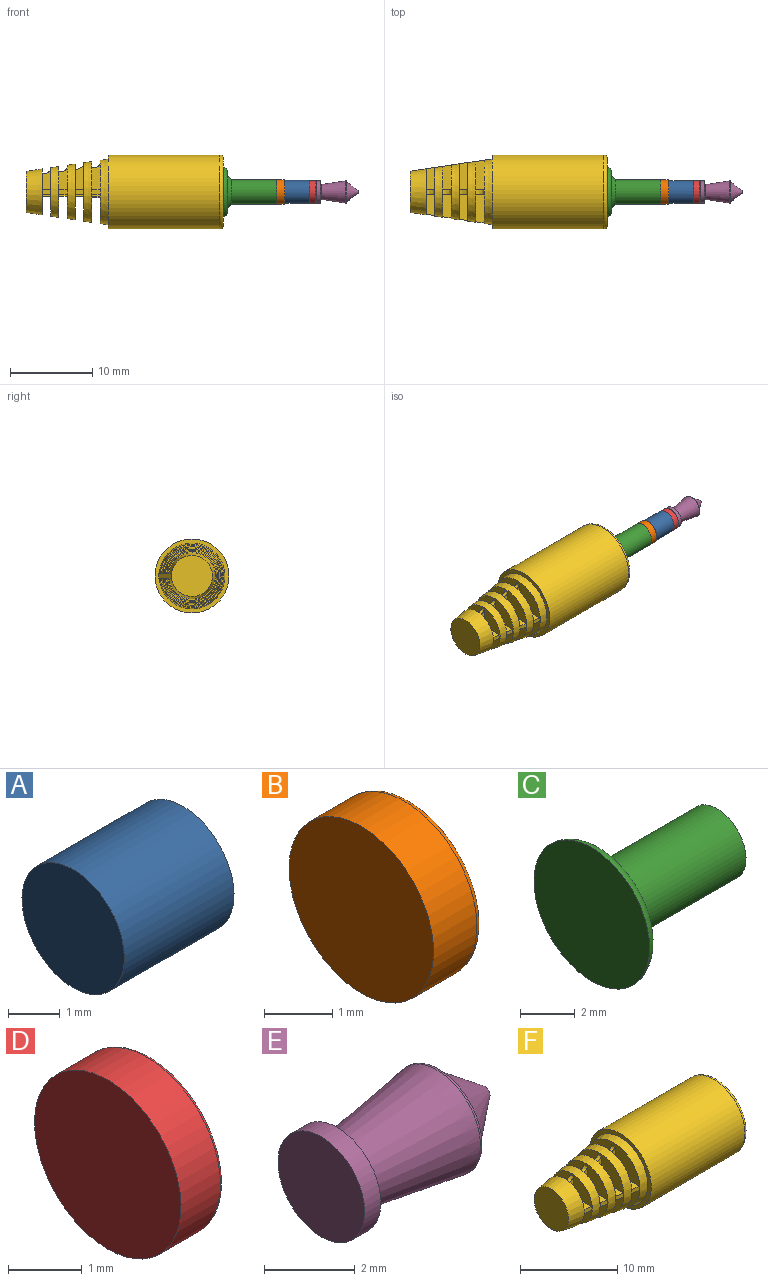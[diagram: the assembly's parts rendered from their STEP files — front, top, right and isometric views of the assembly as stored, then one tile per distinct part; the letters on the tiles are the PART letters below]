
ASSEMBLY  parts=6 mates=5
PART A: 3 faces, bbox 3x2.8x2.8 mm
  f0: cylinder r=1.4mm len=3mm, axis (-1,0,0), area 26.4mm2, adj f1,f2
  f1: plane 2.8x2.8mm, normal (1,0,0), area 6.2mm2, adj f0
  f2: plane 2.8x2.8mm, normal (-1,0,0), area 6.2mm2, adj f0
PART B: 4 faces, bbox 1x3.2x3.2 mm
  f0: cylinder r=1.5mm len=3mm, axis (-1,0,0), area 8.5mm2, adj f2,f3
  f1: plane 2.8x2.8mm, normal (1,0,0), area 6.2mm2, adj f3
  f2: plane 3x3mm, normal (-1,0,0), area 7.1mm2, adj f0
  f3: torus R=1.4mm, axis (1,0,0), area 1.4mm2, adj f0,f1
PART C: 6 faces, bbox 6.6x6.5x6.5 mm
  f0: plane 4.9x4.9mm, normal (1,0,0), area 6.3mm2, adj f4,f5
  f1: plane 6x6mm, normal (-1,0,0), area 28.3mm2, adj f4
  f2: cylinder r=1.5mm len=5.5mm, axis (-1,0,0), area 51.8mm2, adj f3,f5
  f3: plane 3x3mm, normal (1,0,0), area 7.1mm2, adj f2
  f4: torus R=2.45mm, axis (-1,0,0), area 14.3mm2, adj f0,f1
  f5: cone r=1.5mm half-angle=45deg, axis (-1,0,0), area 7.8mm2, adj f0,f2
PART D: 4 faces, bbox 0.8x3x3 mm
  f0: cylinder r=1.4mm len=2.8mm, axis (-1,0,0), area 6.6mm2, adj f2,f3
  f1: plane 2.7x2.7mm, normal (1,0,0), area 5.7mm2, adj f3
  f2: plane 2.8x2.8mm, normal (-1,0,0), area 6.2mm2, adj f0
  f3: torus R=1.35mm, axis (1,0,0), area 0.7mm2, adj f0,f1
PART E: 8 faces, bbox 5.1x2.7x2.7 mm
  f0: plane 2.7x2.7mm, normal (-1,0,0), area 5.7mm2, adj f7
  f1: plane 0.3x0.3mm, normal (1,0,0), area 0.1mm2, adj f2
  f2: cone r=1.28mm half-angle=37.9deg, axis (-1,0,0), area 8.3mm2, adj f1,f3
  f3: plane 2.7x2.7mm, normal (1,0,0), area 0.6mm2, adj f2,f4
  f4: cylinder r=1.35mm len=2.7mm, axis (-1,0,0), area 0.4mm2, adj f3,f5
  f5: cone r=1.35mm half-angle=8.5deg, axis (1,0,0), area 21.4mm2, adj f4,f6
  f6: cone r=1.35mm half-angle=77.5deg, axis (-1,0,0), area 3.3mm2, adj f5,f7
  f7: cylinder r=1.35mm len=2.7mm, axis (-1,0,0), area 4.2mm2, adj f0,f6
PART F: 63 faces, bbox 24x9.7x9.7 mm
  f0: plane 1.01x0.5mm, normal (-0.15,-0.99,0), area 0.5mm2, adj f1,f2,f50,f59
  f1: plane 9.86x6.9mm, normal (0,0,1), area 15.3mm2, adj f0,f28,f32,f33,f35,f38,f39,f42
  f2: plane 9.86x6.9mm, normal (0,0,-1), area 15.3mm2, adj f0,f23,f24,f25,f26,f27,f28,f32
  f3: plane 1x0.14mm, normal (0,-1,0), area 0.1mm2, adj f5,f15,f35,f39
  f4: plane 1x0.14mm, normal (0,1,0), area 0.1mm2, adj f5,f16,f35,f39
  f5: plane 1x0.23mm, normal (0,0,-1), area 0.2mm2, adj f3,f4,f35,f39
  f6: plane 1x0.5mm, normal (-0.15,-0.99,0), area 0.5mm2, adj f11,f12,f35,f39
  f7: plane 1x0.5mm, normal (-0.15,-0.99,0), area 0.5mm2, adj f9,f13,f47,f51
  f8: plane 1.02x0.5mm, normal (-0.15,-0.99,0), area 0.5mm2, adj f10,f14,f48,f52
  f9: plane 2.92x1mm, normal (0,0,1), area 2.8mm2, adj f7,f44,f47,f51
  f10: plane 3.22x1.02mm, normal (0,0,1), area 3.2mm2, adj f8,f41,f48,f52
  f11: plane 3.52x1mm, normal (0,0,1), area 3.4mm2, adj f6,f35,f37,f39
  f12: plane 3.52x1mm, normal (0,0,-1), area 3.4mm2, adj f6,f20,f35,f39
  f13: plane 2.92x1mm, normal (0,0,-1), area 2.8mm2, adj f7,f21,f47,f51
  f14: plane 3.22x1.02mm, normal (0,0,-1), area 3.2mm2, adj f8,f22,f48,f52
  f15: plane 1x0.25mm, normal (0,0,-1), area 0.3mm2, adj f3,f20,f35,f39
  f16: plane 1x0.02mm, normal (0,0,-1), area 0mm2, adj f4,f24,f35,f39
  f17: plane 1x0.5mm, normal (0,0,-1), area 0.5mm2, adj f21,f25,f47,f51
  f18: plane 1.02x0.5mm, normal (0,0,-1), area 0.5mm2, adj f22,f26,f48,f52
  f19: plane 0.99x0.5mm, normal (0,0,-1), area 0.5mm2, adj f23,f27,f34,f50
  f20: plane 1x0.3mm, normal (0,-1,0), area 0.3mm2, adj f12,f15,f35,f39
  f21: plane 1x0.3mm, normal (0,-1,0), area 0.3mm2, adj f13,f17,f47,f51
  f22: plane 1.02x0.3mm, normal (0,-1,0), area 0.3mm2, adj f14,f18,f48,f52
  f23: plane 0.99x0.3mm, normal (0,-1,0), area 0.3mm2, adj f2,f19,f34,f50
  f24: plane 1x0.3mm, normal (0,1,0), area 0.3mm2, adj f2,f16,f35,f39
  f25: plane 1x0.3mm, normal (0,1,0), area 0.3mm2, adj f2,f17,f47,f51
  f26: plane 1.02x0.3mm, normal (0,1,0), area 0.3mm2, adj f2,f18,f48,f52
  f27: plane 0.99x0.3mm, normal (0,1,0), area 0.3mm2, adj f2,f19,f34,f50
  f28: plane 9x9mm, normal (-1,0,0), area 13.3mm2, adj f1,f2,f29,f32,f54
  f29: cylinder r=4.5mm len=13.6mm, axis (1,0,0), area 384.5mm2, adj f28,f31
  f30: plane 8.2x8.2mm, normal (1,0,0), area 52.8mm2, adj f31
  f31: torus R=4.1mm, axis (1,0,0), area 17.2mm2, adj f29,f30
  f32: plane 9.85x1.48mm, normal (-0.15,0.99,0), area 5mm2, adj f1,f2,f28,f33
  f33: plane 0.5x0.04mm, normal (-1,0,0), area 0mm2, adj f1,f2,f32,f61
  f34: plane 0.5x0.3mm, normal (-1,0,0), area 0.2mm2, adj f2,f19,f23,f27
  f35: plane 7.7x7.69mm, normal (-1,0,0), area 40.9mm2, adj f1,f2,f3,f4,f5,f6,f11,f12
  f36: extruded ~1x0.52mm, area 0.6mm2, adj f35,f37,f38,f39
  f37: plane 3.25x1mm, normal (0,-1,0), area 2.8mm2, adj f11,f35,f36,f39
  f38: plane 3.25x1mm, normal (0,1,0), area 2.8mm2, adj f1,f35,f36,f39
  f39: plane 7.4x7.39mm, normal (1,0,0), area 37.8mm2, adj f1,f2,f3,f4,f5,f6,f11,f12
  f40: extruded ~1.02x0.51mm, area 0.6mm2, adj f41,f42,f48,f52
  f41: plane 3x1.02mm, normal (0,-1,0), area 2.7mm2, adj f10,f40,f48,f52
  f42: plane 3x1.02mm, normal (0,1,0), area 2.7mm2, adj f1,f40,f48,f52
  f43: extruded ~1x0.51mm, area 0.6mm2, adj f44,f45,f47,f51
  f44: plane 2.75x1mm, normal (0,-1,0), area 2.3mm2, adj f9,f43,f47,f51
  f45: plane 2.75x1mm, normal (0,1,0), area 2.3mm2, adj f1,f43,f47,f51
  f46: cone r=3.4mm half-angle=8.5deg, axis (1,0,0), area 20.6mm2, adj f1,f2,f47,f48
  f47: plane 6.5x6.49mm, normal (-1,0,0), area 28.4mm2, adj f1,f2,f7,f9,f13,f17,f21,f25
  f48: plane 6.8x6.79mm, normal (1,0,0), area 31.6mm2, adj f1,f2,f8,f10,f14,f18,f22,f26
  f49: cone r=3.09mm half-angle=8deg, axis (1,0,0), area 18.5mm2, adj f1,f2,f50,f51
  f50: plane 5.9x5.89mm, normal (-1,0,0), area 24.3mm2, adj f0,f1,f2,f19,f23,f27,f49
  f51: plane 6.18x6.17mm, normal (1,0,0), area 25.7mm2, adj f1,f2,f7,f9,f13,f17,f21,f25
  f52: plane 7.1x7.09mm, normal (-1,0,0), area 34.4mm2, adj f1,f2,f8,f10,f14,f18,f22,f26
  f53: cone r=3.7mm half-angle=8.5deg, axis (1,0,0), area 22.5mm2, adj f1,f2,f39,f52
  f54: cone r=4mm half-angle=8.5deg, axis (1,0,0), area 24.4mm2, adj f1,f2,f28,f35
  f55: plane 2.5x0.5mm, normal (1,0,0), area 1.2mm2, adj f1,f56,f57,f58
  f56: extruded ~1x0.52mm, area 0.6mm2, adj f55,f57,f58,f59
  f57: plane 2.5x1mm, normal (0,-1,0), area 2.1mm2, adj f1,f55,f56,f59
  f58: plane 2.5x1mm, normal (0,1,0), area 2.1mm2, adj f1,f55,f56,f59
  f59: plane 5.6x5.59mm, normal (1,0,0), area 20.9mm2, adj f0,f1,f2,f56,f57,f58,f61,f62
  f60: plane 5x5mm, normal (-1,0,0), area 19.6mm2, adj f61
  f61: cone r=2.8mm half-angle=8.5deg, axis (1,0,0), area 32.7mm2, adj f1,f33,f59,f60,f62
  f62: cone r=2.8mm half-angle=8.5deg, axis (1,0,0), area 0mm2, adj f2,f59,f61
PLACE A t=(-1,0,0)mm
PLACE B t=(-1,0,0)mm
PLACE C t=(-1,0,0)mm
PLACE D t=(-1,0,0)mm
PLACE E t=(-1,0,0)mm
PLACE F t=(-1,0,0)mm
MATE fastened F.f29 <-> C.f4  axis (1,0,0) through (-1,0,0)mm
MATE fastened E.f6 <-> D.f0  axis (-1,0,0) through (10.3,0,0)mm
MATE fastened D.f0 <-> A.f0  axis (-1,0,0) through (9.5,0,0)mm
MATE fastened B.f0 <-> C.f2  axis (-1,0,0) through (5.5,0,0)mm
MATE fastened A.f0 <-> B.f0  axis (-1,0,0) through (6.5,0,0)mm
